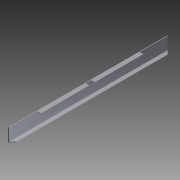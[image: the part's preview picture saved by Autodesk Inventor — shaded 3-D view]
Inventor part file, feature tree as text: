
AUTODESK INVENTOR PART (.ipt)
format: ipt  version: 2012 (Build 160160000, 160)  size: 111,616 bytes
history: native  units: in
note: dims shown in document units (in); Inventor stores cm internally (conversion verified against a paired STEP export)
features: extrude x4, sketch x3
ambient origin geometry x8: Origin, YZ Plane, XZ Plane, XY Plane, X Axis, Y Axis, Z Axis, Center Point
bodies: Solid1 (feature_tree)
feature tree (7):
  extrude  "Extrusion1"  Depth=1.0in
  sketch  "Sketch2"  dims[d2=0.125in d3=0.125in]
  extrude  "Extrusion2"  Depth=0.125in
  extrude  "Extrusion3"  Depth=37.0in TaperAngle=0.0deg
  extrude  "Extrusion4"  TaperAngle=45.0deg  [1 undecoded]
  sketch  "Sketch1"  dims[d0=3.0in d1=1.0in]
  sketch  "Sketch3"  dims[d4=0.125in d5=37.0in d6=0.0in d7=45.0deg d8=0.125in d9=6.5in d10=6.5in d11=28.0in d12=0.0in d13=28.0in d14=0.0in d15=1.25in d16=0.875in d17=17.875in d18=1.0in d19=0.0in]
note: 1 required parameter value undecoded (feature->parameter linkage not recoverable at this tier; creation-order binding heuristic only, values carry confidence <= 0.55)
